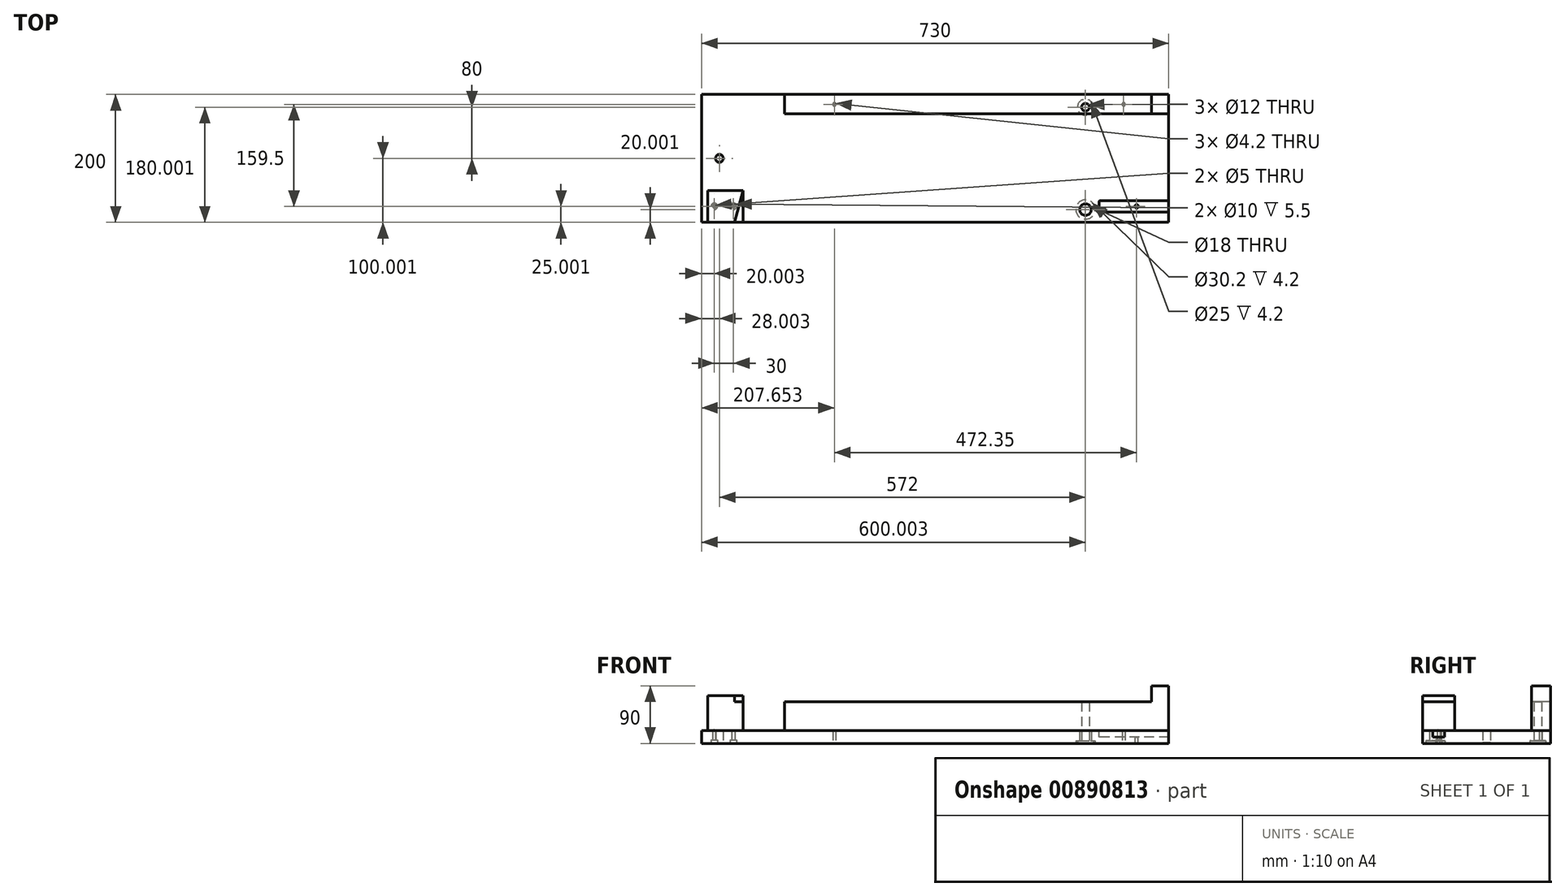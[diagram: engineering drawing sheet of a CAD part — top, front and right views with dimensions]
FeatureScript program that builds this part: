
annotation { "Feature Type Name" : "Feature", "Feature Type Description" : "" }
export const myFeature = defineFeature(function(context is Context, id is Id, definition is map)
    precondition{}
    {
        {
            var Q0;
            Q0=qCreatedBy(makeId("Top.planeOp"),FACE);
            var sketch = newSketch(context, id + "F0", { "sketchPlane" : qUnion([Q0])});
            skLineSegment(sketch, "E0.bottom", {"start": v(-675.18, 188.43) * mm, "end": v(54.82, 188.43) * mm});
            skLineSegment(sketch, "E0.top", {"start": v(-675.18, -11.57) * mm, "end": v(54.82, -11.57) * mm});
            skLineSegment(sketch, "E0.left", {"start": v(-675.18, 188.43) * mm, "end": v(-675.18, -11.57) * mm});
            skLineSegment(sketch, "E0.right", {"start": v(54.82, 188.43) * mm, "end": v(54.82, -11.57) * mm});
            skSolve(sketch);
        }
        {
            var Q0;
            Q0=makeQuery(id+"F0.imprint","IMPRINT",FACE,{"disambiguationData":[TD([[makeQuery(id+"F0.imprint","IMPRINT",EDGE,{"derivedFrom":sQuery(id+"F0.wireOp",EDGE,"E0.bottom")}),-1.0]])]});
            extrude(context, id + "F1", {"entities" : qUnion([Q0]), "depth" : 20 * mm, "offsetDistance" : 25 * mm});
        }
        {
            var Q0;
            Q0=makeQuery(id+"F1.opExtrude","CAP_FACE",FACE,{"disambiguationData":[OSD([sQuery(id+"F0.wireOp",EDGE,"E0.bottom"),sQuery(id+"F0.wireOp",EDGE,"E0.top"),sQuery(id+"F0.wireOp",EDGE,"E0.left"),sQuery(id+"F0.wireOp",EDGE,"E0.right")])],"isStart":false});
            var sketch = newSketch(context, id + "F2", { "sketchPlane" : qUnion([Q0])});
            skLineSegment(sketch, "E1.bottom", {"start": v(54.82, 188.43) * mm, "end": v(-545.18, 188.43) * mm});
            skLineSegment(sketch, "E1.top", {"start": v(54.82, 158.43) * mm, "end": v(-545.18, 158.43) * mm});
            skLineSegment(sketch, "E1.left", {"start": v(54.82, 188.43) * mm, "end": v(54.82, 158.43) * mm});
            skLineSegment(sketch, "E1.right", {"start": v(-545.18, 188.43) * mm, "end": v(-545.18, 158.43) * mm});
            skSolve(sketch);
        }
        {
            var Q0;
            Q0=makeQuery(id+"F2.imprint","IMPRINT",FACE,{"disambiguationData":[TD([[makeQuery(id+"F2.imprint","IMPRINT",EDGE,{"derivedFrom":sQuery(id+"F2.wireOp",EDGE,"E1.bottom")}),-1.0]])]});
            extrude(context, id + "F3", {"entities" : qUnion([Q0]), "depth" : 45 * mm, "offsetDistance" : 25 * mm});
        }
        {
            var Q0;
            Q0=makeQuery(id+"F3.opExtrude","CAP_FACE",FACE,{"disambiguationData":[OSD([sQuery(id+"F2.wireOp",EDGE,"E1.bottom"),sQuery(id+"F2.wireOp",EDGE,"E1.top"),sQuery(id+"F2.wireOp",EDGE,"E1.left"),sQuery(id+"F2.wireOp",EDGE,"E1.right")])],"isStart":false});
            var sketch = newSketch(context, id + "F4", { "sketchPlane" : qUnion([Q0])});
            skLineSegment(sketch, "E2.bottom", {"start": v(54.82, 188.43) * mm, "end": v(27.82, 188.43) * mm});
            skLineSegment(sketch, "E2.top", {"start": v(54.82, 158.43) * mm, "end": v(27.82, 158.43) * mm});
            skLineSegment(sketch, "E2.left", {"start": v(54.82, 188.43) * mm, "end": v(54.82, 158.43) * mm});
            skLineSegment(sketch, "E2.right", {"start": v(27.82, 188.43) * mm, "end": v(27.82, 158.43) * mm});
            skSolve(sketch);
        }
        {
            var Q0;
            Q0=makeQuery(id+"F4.imprint","IMPRINT",FACE,{"disambiguationData":[TD([[makeQuery(id+"F4.imprint","IMPRINT",EDGE,{"derivedFrom":sQuery(id+"F4.wireOp",EDGE,"E2.bottom")}),-1.0]])]});
            extrude(context, id + "F5", {"entities" : qUnion([Q0]), "operationType" : NewBodyOperationType.ADD, "depth" : 25 * mm, "offsetDistance" : 25 * mm});
        }
        {
            var Q0;
            Q0=makeQuery(id+"F1.opExtrude","CAP_FACE",FACE,{"disambiguationData":[OSD([sQuery(id+"F0.wireOp",EDGE,"E0.bottom"),sQuery(id+"F0.wireOp",EDGE,"E0.top"),sQuery(id+"F0.wireOp",EDGE,"E0.left"),sQuery(id+"F0.wireOp",EDGE,"E0.right")])],"isStart":false});
            var sketch = newSketch(context, id + "F6", { "sketchPlane" : qUnion([Q0])});
            skLineSegment(sketch, "E3.bottom", {"start": v(-665.18, -11.57) * mm, "end": v(-610.48, -11.57) * mm});
            skLineSegment(sketch, "E3.top", {"start": v(-665.18, 38.43) * mm, "end": v(-610.48, 38.43) * mm});
            skLineSegment(sketch, "E3.right", {"start": v(-610.48, -11.57) * mm, "end": v(-610.48, 38.43) * mm});
            skLineSegment(sketch, "E4.0", {"start": v(-665.18, -11.57) * mm, "end": v(-665.18, 38.43) * mm});
            skSolve(sketch);
        }
        {
            var Q0;
            Q0=makeQuery(id+"F6.imprint","IMPRINT",FACE,{"disambiguationData":[TD([[makeQuery(id+"F6.imprint","IMPRINT",EDGE,{"derivedFrom":sQuery(id+"F6.wireOp",EDGE,"E3.bottom")}),1.0]])]});
            extrude(context, id + "F7", {"entities" : qUnion([Q0]), "depth" : 45 * mm, "offsetDistance" : 25 * mm});
        }
        {
            var Q0;
            Q0=makeQuery(id+"F7.opExtrude","CAP_FACE",FACE,{"disambiguationData":[OSD([sQuery(id+"F6.wireOp",EDGE,"E3.bottom"),sQuery(id+"F6.wireOp",EDGE,"E3.top"),sQuery(id+"F6.wireOp",EDGE,"E3.left"),sQuery(id+"F6.wireOp",EDGE,"E3.right")])],"isStart":false});
            var sketch = newSketch(context, id + "F8", { "sketchPlane" : qUnion([Q0])});
            skLineSegment(sketch, "E5", {"start": v(-665.18, 38.43) * mm, "end": v(-610.48, 38.43) * mm});
            skLineSegment(sketch, "E6", {"start": v(-665.18, -11.57) * mm, "end": v(-665.18, 38.43) * mm});
            skLineSegment(sketch, "E7", {"start": v(-665.18, -11.57) * mm, "end": v(-623.58, -11.57) * mm});
            skLineSegment(sketch, "E8", {"start": v(-610.48, 38.43) * mm, "end": v(-623.58, -11.57) * mm});
            skSolve(sketch);
        }
        {
            var Q0;
            Q0=makeQuery(id+"F8.imprint","IMPRINT",FACE,{"disambiguationData":[TD([[makeQuery(id+"F8.imprint","IMPRINT",EDGE,{"derivedFrom":sQuery(id+"F8.wireOp",EDGE,"E5")}),-1.0]])]});
            extrude(context, id + "F9", {"entities" : qUnion([Q0]), "operationType" : NewBodyOperationType.ADD, "depth" : 10 * mm, "offsetDistance" : 25 * mm});
        }
        {
            var Q0;
            Q0=makeQuery(id+"F1.opExtrude","CAP_FACE",FACE,{"disambiguationData":[OSD([sQuery(id+"F0.wireOp",EDGE,"E0.bottom"),sQuery(id+"F0.wireOp",EDGE,"E0.top"),sQuery(id+"F0.wireOp",EDGE,"E0.left"),sQuery(id+"F0.wireOp",EDGE,"E0.right")])],"isStart":false});
            var sketch = newSketch(context, id + "F10", { "sketchPlane" : qUnion([Q0])});
            skLineSegment(sketch, "E9", {"start": v(54.82, 13.43) * mm, "end": v(-82.04, 13.43) * mm, "construction": true});
            skLineSegment(sketch, "E10.0", {"start": v(57.24, 22.43) * mm, "end": v(-52.18, 22.43) * mm});
            skLineSegment(sketch, "E11.0", {"start": v(57.24, 4.43) * mm, "end": v(-52.18, 4.43) * mm});
            skLineSegment(sketch, "E12", {"start": v(57.24, 22.43) * mm, "end": v(57.24, 4.43) * mm});
            skLineSegment(sketch, "E13", {"start": v(-54.18, 20.43) * mm, "end": v(-54.18, 6.43) * mm});
            skPoint(sketch, "E14.visualSharp", {"position": v(-54.18, 22.43) * mm});
            skArc(sketch, "E14.filletArc", {"start": v(-52.18, 22.43) * mm, "mid": v(-53.6, 21.84) * mm, "end": v(-54.18, 20.43) * mm});
            skPoint(sketch, "E15.visualSharp", {"position": v(-54.18, 4.43) * mm});
            skArc(sketch, "E15.filletArc", {"start": v(-54.18, 6.43) * mm, "mid": v(-53.6, 5.02) * mm, "end": v(-52.18, 4.43) * mm});
            skSolve(sketch);
        }
        {
            var Q0;
            Q0=makeQuery(id+"F10.imprint","IMPRINT",FACE,{"disambiguationData":[TD([[makeQuery(id+"F10.imprint","IMPRINT",EDGE,{"derivedFrom":sQuery(id+"F10.wireOp",EDGE,"E13")}),1.0]])]});
            extrude(context, id + "F11", {"entities" : qUnion([Q0]), "operationType" : NewBodyOperationType.REMOVE, "oppositeDirection" : true, "depth" : 10 * mm, "offsetDistance" : 25 * mm});
        }
        {
            var Q0;
            Q0=makeQuery(id+"F11.boolean.opBoolean","COPY",FACE,{"derivedFrom":makeQuery(id+"F11.opExtrude","CAP_FACE",FACE,{"disambiguationData":[OSD([sQuery(id+"F0.wireOp",EDGE,"E0.right"),sQuery(id+"F10.wireOp",EDGE,"E10.0"),sQuery(id+"F10.wireOp",EDGE,"E11.0"),sQuery(id+"F10.wireOp",EDGE,"E13"),sQuery(id+"F10.wireOp",EDGE,"E14.filletArc"),sQuery(id+"F10.wireOp",EDGE,"E15.filletArc")])],"isStart":false})});
            var sketch = newSketch(context, id + "F12", { "sketchPlane" : qUnion([Q0])});
            skLineSegment(sketch, "E16", {"start": v(-59.39, 13.43) * mm, "end": v(59.1, 13.43) * mm, "construction": true});
            skLineSegment(sketch, "E17", {"start": v(4.82, 22.43) * mm, "end": v(4.82, 4.43) * mm, "construction": true});
            skPoint(sketch, "E18", {"position": v(4.82, 13.43) * mm});
            skSolve(sketch);
        }
        {
            var Q0;
            Q0=sQuery(id+"F12.wireOp",VERTEX,"E18");
            var Q1;
            Q1=makeQuery(id+"F1.opExtrude","SWEPT_BODY",BODY,{"disambiguationData":[OSD([sQuery(id+"F0.wireOp",EDGE,"E0.bottom"),sQuery(id+"F0.wireOp",EDGE,"E0.top"),sQuery(id+"F0.wireOp",EDGE,"E0.left"),sQuery(id+"F0.wireOp",EDGE,"E0.right")])]});
            hole(context, id + "F13", {"style" : HoleStyle.C_SINK, "endStyle" : HoleEndStyle.THROUGH, "holeDiameter" : 4.2 * mm, "cSinkDiameter" : 5.5 * mm, "cSinkAngle" : 90 * degree, "majorDiameter" : 5 * mm, "isTappedThrough" : true, "tappedDepth" : 12 * mm, "tapClearance" : 3, "locations" : qUnion([Q0]), "scope" : qUnion([Q1])});
        }
        {
            var Q0;
            Q0=makeQuery(id+"F1.opExtrude","CAP_FACE",FACE,{"disambiguationData":[OSD([sQuery(id+"F0.wireOp",EDGE,"E0.bottom"),sQuery(id+"F0.wireOp",EDGE,"E0.top"),sQuery(id+"F0.wireOp",EDGE,"E0.left"),sQuery(id+"F0.wireOp",EDGE,"E0.right")])],"isStart":true});
            var sketch = newSketch(context, id + "F14", { "sketchPlane" : qUnion([Q0])});
            skLineSegment(sketch, "E19", {"start": v(54.82, -172.93) * mm, "end": v(-675.18, -172.93) * mm, "construction": true});
            skLineSegment(sketch, "E20", {"start": v(-15.53, -139.46) * mm, "end": v(-15.53, -178.23) * mm, "construction": true});
            skLineSegment(sketch, "E21", {"start": v(-467.53, -140.35) * mm, "end": v(-467.53, -178.23) * mm, "construction": true});
            skPoint(sketch, "E22", {"position": v(-15.53, -172.93) * mm});
            skPoint(sketch, "E23", {"position": v(-467.53, -172.93) * mm});
            skPoint(sketch, "E24", {"position": v(-647.18, -88.43) * mm});
            skLineSegment(sketch, "E25", {"start": v(-605.41, -88.43) * mm, "end": v(-683.85, -88.43) * mm, "construction": true});
            skLineSegment(sketch, "E26", {"start": v(-675.18, -13.43) * mm, "end": v(-600.75, -13.43) * mm, "construction": true});
            skPoint(sketch, "E27", {"position": v(-655.18, -13.43) * mm});
            skPoint(sketch, "E28", {"position": v(-625.18, -13.43) * mm});
            skSolve(sketch);
        }
        {
            var Q0;
            Q0=sQuery(id+"F14.wireOp",VERTEX,"E22");
            var Q1;
            Q1=sQuery(id+"F14.wireOp",VERTEX,"E23");
            var Q2;
            Q2=makeQuery(id+"F7.opExtrude","SWEPT_BODY",BODY,{"disambiguationData":[OSD([sQuery(id+"F6.wireOp",EDGE,"E3.bottom"),sQuery(id+"F6.wireOp",EDGE,"E3.top"),sQuery(id+"F6.wireOp",EDGE,"E3.right"),sQuery(id+"F6.wireOp",EDGE,"E4.0")])]});
            var Q3;
            Q3=makeQuery(id+"F1.opExtrude","SWEPT_BODY",BODY,{"disambiguationData":[OSD([sQuery(id+"F0.wireOp",EDGE,"E0.bottom"),sQuery(id+"F0.wireOp",EDGE,"E0.top"),sQuery(id+"F0.wireOp",EDGE,"E0.left"),sQuery(id+"F0.wireOp",EDGE,"E0.right")])]});
            hole(context, id + "F15", {"style" : HoleStyle.C_SINK, "endStyle" : HoleEndStyle.THROUGH, "holeDiameter" : 4.2 * mm, "cSinkDiameter" : 5.2 * mm, "cSinkAngle" : 90 * degree, "majorDiameter" : 5 * mm, "isTappedThrough" : true, "tappedDepth" : 12 * mm, "tapClearance" : 3, "locations" : qUnion([Q0, Q1]), "scope" : qUnion([Q2, Q3])});
        }
        {
            var Q0;
            Q0=sQuery(id+"F14.wireOp",VERTEX,"E24");
            var Q1;
            Q1=makeQuery(id+"F1.opExtrude","SWEPT_BODY",BODY,{"disambiguationData":[OSD([sQuery(id+"F0.wireOp",EDGE,"E0.bottom"),sQuery(id+"F0.wireOp",EDGE,"E0.top"),sQuery(id+"F0.wireOp",EDGE,"E0.left"),sQuery(id+"F0.wireOp",EDGE,"E0.right")])]});
            hole(context, id + "F16", {"style" : HoleStyle.C_SINK, "endStyle" : HoleEndStyle.THROUGH, "holeDiameter" : 12 * mm, "cSinkDiameter" : 14.2 * mm, "cSinkAngle" : 90 * degree, "majorDiameter" : 5 * mm, "isTappedThrough" : true, "tappedDepth" : 12 * mm, "tapClearance" : 3, "locations" : qUnion([Q0]), "scope" : qUnion([Q1])});
        }
        {
            var Q0;
            Q0=sQuery(id+"F14.wireOp",VERTEX,"E27");
            var Q1;
            Q1=sQuery(id+"F14.wireOp",VERTEX,"E28");
            var Q2;
            Q2=makeQuery(id+"F7.opExtrude","SWEPT_BODY",BODY,{"disambiguationData":[OSD([sQuery(id+"F6.wireOp",EDGE,"E3.bottom"),sQuery(id+"F6.wireOp",EDGE,"E3.top"),sQuery(id+"F6.wireOp",EDGE,"E3.right"),sQuery(id+"F6.wireOp",EDGE,"E4.0")])]});
            var Q3;
            Q3=makeQuery(id+"F1.opExtrude","SWEPT_BODY",BODY,{"disambiguationData":[OSD([sQuery(id+"F0.wireOp",EDGE,"E0.bottom"),sQuery(id+"F0.wireOp",EDGE,"E0.top"),sQuery(id+"F0.wireOp",EDGE,"E0.left"),sQuery(id+"F0.wireOp",EDGE,"E0.right")])]});
            hole(context, id + "F17", {"style" : HoleStyle.C_BORE, "endStyle" : HoleEndStyle.BLIND, "holeDiameter" : 5 * mm, "cBoreDiameter" : 10 * mm, "cBoreDepth" : 5.5 * mm, "majorDiameter" : 5 * mm, "holeDepth" : 20 * mm, "isTappedThrough" : true, "tappedDepth" : 12 * mm, "tapClearance" : 3, "locations" : qUnion([Q0, Q1]), "scope" : qUnion([Q2, Q3])});
        }
        {
            var Q0;
            Q0=makeQuery(id+"F1.opExtrude","CAP_FACE",FACE,{"disambiguationData":[OSD([sQuery(id+"F0.wireOp",EDGE,"E0.bottom"),sQuery(id+"F0.wireOp",EDGE,"E0.top"),sQuery(id+"F0.wireOp",EDGE,"E0.left"),sQuery(id+"F0.wireOp",EDGE,"E0.right")])],"isStart":true});
            var sketch = newSketch(context, id + "F18", { "sketchPlane" : qUnion([Q0])});
            skLineSegment(sketch, "E29", {"start": v(-75.18, 96.27) * mm, "end": v(-75.18, -294.97) * mm, "construction": true});
            skCircle(sketch, "E30", {"center": v(-75.18, -8.43) * mm, "radius": 9 * mm});
            skCircle(sketch, "E31", {"center": v(-75.18, -168.43) * mm, "radius": 6 * mm});
            skCircle(sketch, "E32", {"center": v(-75.18, -8.43) * mm, "radius": 13 * mm, "construction": true});
            skSolve(sketch);
        }
        {
            var Q0;
            Q0=makeQuery(id+"F18.imprint","IMPRINT",FACE,{"disambiguationData":[TD([[makeQuery(id+"F18.imprint","IMPRINT",EDGE,{"derivedFrom":sQuery(id+"F18.wireOp",EDGE,"E30")}),1.0]])]});
            var Q1;
            Q1=makeQuery(id+"F18.imprint","IMPRINT",FACE,{"disambiguationData":[TD([[makeQuery(id+"F18.imprint","IMPRINT",EDGE,{"derivedFrom":sQuery(id+"F18.wireOp",EDGE,"E31")}),1.0]])]});
            extrude(context, id + "F19", {"entities" : qUnion([Q0, Q1]), "operationType" : NewBodyOperationType.REMOVE, "endBound" : BoundingType.THROUGH_ALL, "oppositeDirection" : true, "depth" : 25 * mm, "offsetDistance" : 25 * mm});
        }
        {
            var Q0;
            Q0=makeQuery(id+"F1.opExtrude","CAP_FACE",FACE,{"disambiguationData":[OSD([sQuery(id+"F0.wireOp",EDGE,"E0.bottom"),sQuery(id+"F0.wireOp",EDGE,"E0.top"),sQuery(id+"F0.wireOp",EDGE,"E0.left"),sQuery(id+"F0.wireOp",EDGE,"E0.right")])],"isStart":true});
            var sketch = newSketch(context, id + "F20", { "sketchPlane" : qUnion([Q0])});
            skCircle(sketch, "E33", {"center": v(-75.18, -8.43) * mm, "radius": 15.1 * mm});
            skCircle(sketch, "E34", {"center": v(-75.18, -168.43) * mm, "radius": 12.5 * mm});
            skSolve(sketch);
        }
        {
            var Q0;
            Q0=makeQuery(id+"F20.imprint","IMPRINT",FACE,{"disambiguationData":[TD([[makeQuery(id+"F20.imprint","IMPRINT",EDGE,{"derivedFrom":sQuery(id+"F20.wireOp",EDGE,"E33")}),1.0]])]});
            var Q1;
            Q1=makeQuery(id+"F20.imprint","IMPRINT",FACE,{"disambiguationData":[TD([[makeQuery(id+"F20.imprint","IMPRINT",EDGE,{"derivedFrom":sQuery(id+"F20.wireOp",EDGE,"E34")}),1.0]])]});
            extrude(context, id + "F21", {"entities" : qUnion([Q0, Q1]), "operationType" : NewBodyOperationType.REMOVE, "oppositeDirection" : true, "depth" : 4.2 * mm, "offsetDistance" : 25 * mm});
        }
    });
